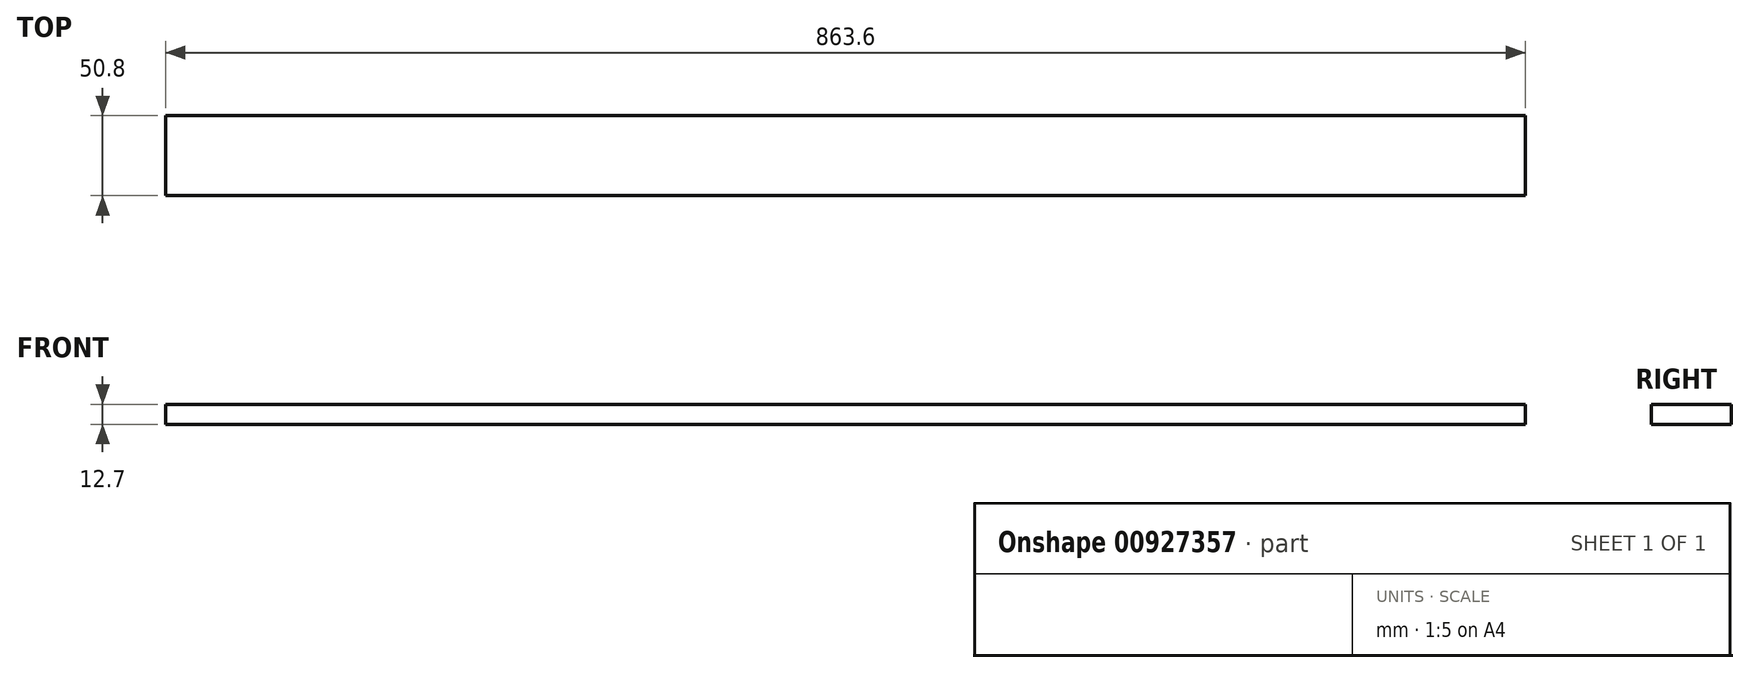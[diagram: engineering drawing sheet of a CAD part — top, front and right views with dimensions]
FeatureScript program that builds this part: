
annotation { "Feature Type Name" : "Feature", "Feature Type Description" : "" }
export const myFeature = defineFeature(function(context is Context, id is Id, definition is map)
    precondition{}
    {
        {
            var Q0;
            Q0=qCreatedBy(makeId("Right.planeOp"),FACE);
            var sketch = newSketch(context, id + "F0", { "sketchPlane" : qUnion([Q0])});
            skLineSegment(sketch, "E0.bottom", {"start": v(-25.4, 6.35) * mm, "end": v(25.4, 6.35) * mm});
            skLineSegment(sketch, "E0.top", {"start": v(-25.4, -6.35) * mm, "end": v(25.4, -6.35) * mm});
            skLineSegment(sketch, "E0.left", {"start": v(-25.4, 6.35) * mm, "end": v(-25.4, -6.35) * mm});
            skLineSegment(sketch, "E0.right", {"start": v(25.4, 6.35) * mm, "end": v(25.4, -6.35) * mm});
            skSolve(sketch);
        }
        {
            var Q0;
            Q0=makeQuery(id+"F0.imprint","IMPRINT",FACE,{"disambiguationData":[TD([[makeQuery(id+"F0.imprint","IMPRINT",EDGE,{"derivedFrom":sQuery(id+"F0.wireOp",EDGE,"E0.bottom")}),-1.0]])]});
            extrude(context, id + "F1", {"entities" : qUnion([Q0]), "depth" : 431.8 * mm, "offsetDistance" : 25.4 * mm, "hasSecondDirection" : true, "secondDirectionOppositeDirection" : true, "secondDirectionDepth" : 431.8 * mm});
        }
    });
